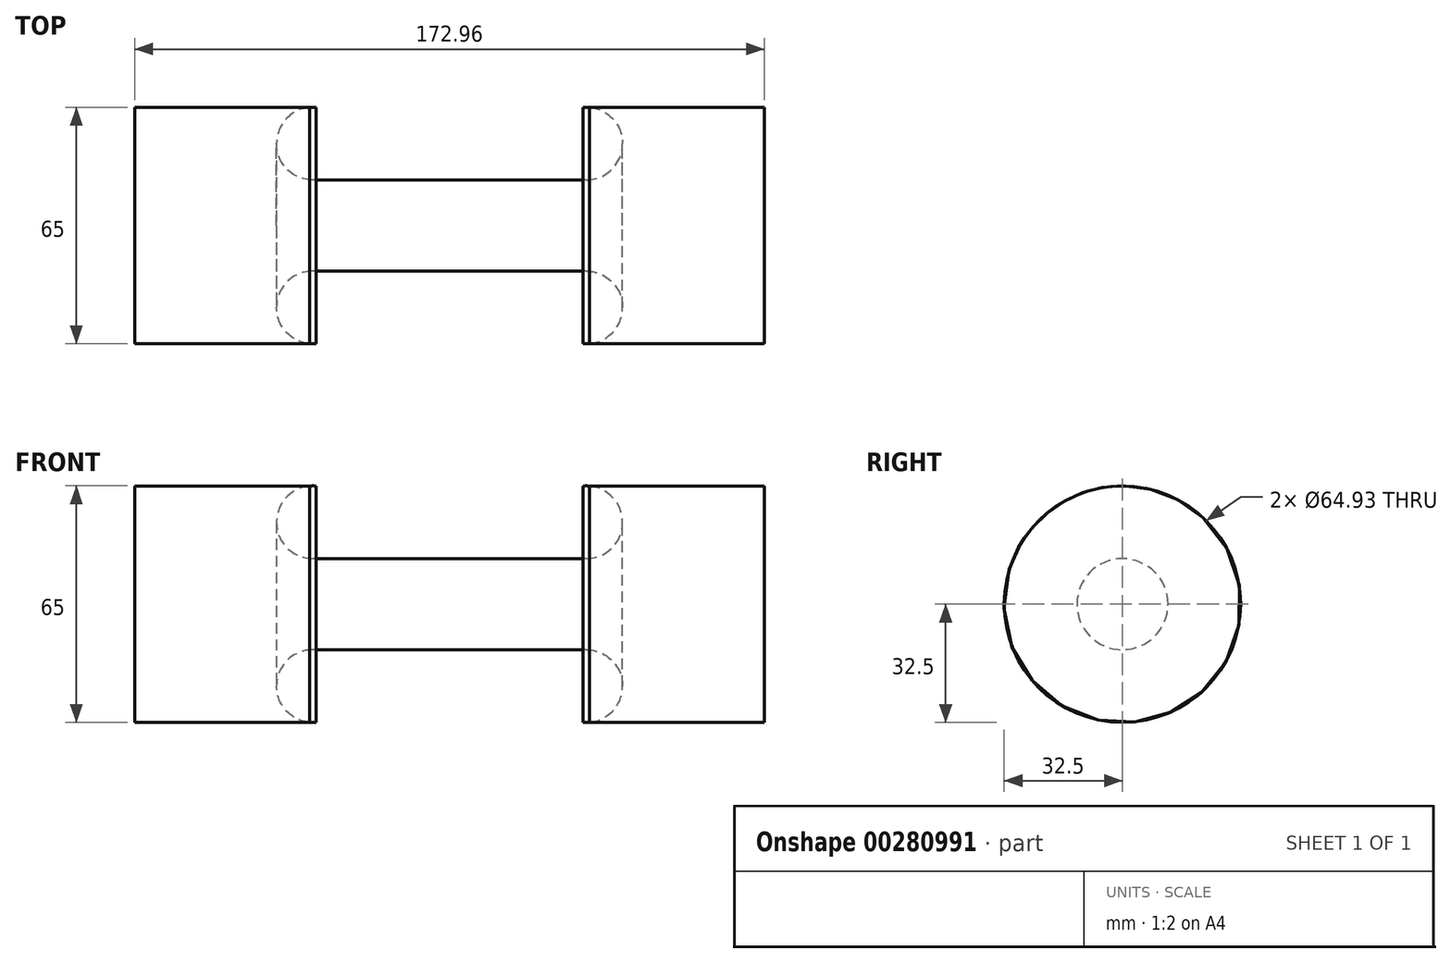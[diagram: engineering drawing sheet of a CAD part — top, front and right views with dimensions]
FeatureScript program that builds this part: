
annotation { "Feature Type Name" : "Feature", "Feature Type Description" : "" }
export const myFeature = defineFeature(function(context is Context, id is Id, definition is map)
    precondition{}
    {
        {
            var Q0;
            Q0=qCreatedBy(makeId("Front.planeOp"),FACE);
            var sketch = newSketch(context, id + "F0", { "sketchPlane" : qUnion([Q0])});
            skLineSegment(sketch, "E0", {"start": v(0, 12.5) * mm, "end": v(37.5, 12.5) * mm});
            skArc(sketch, "E1", {"start": v(37.5, 12.5) * mm, "mid": v(47.5, 22.93) * mm, "end": v(36.64, 32.46) * mm});
            skLineSegment(sketch, "E2", {"start": v(36.64, 32.46) * mm, "end": v(86.48, 32.46) * mm});
            skLineSegment(sketch, "E3", {"start": v(86.48, 32.46) * mm, "end": v(86.48, 0) * mm});
            skArc(sketch, "E4.MirrorCS", {"start": v(-37.5, 12.5) * mm, "mid": v(-47.5, 22.93) * mm, "end": v(-36.64, 32.46) * mm});
            skLineSegment(sketch, "E5.MirrorCS", {"start": v(0, 12.5) * mm, "end": v(-37.5, 12.5) * mm});
            skLineSegment(sketch, "E6.MirrorCS", {"start": v(-86.48, 32.46) * mm, "end": v(-86.48, 0) * mm});
            skLineSegment(sketch, "E7.MirrorCS", {"start": v(-36.64, 32.46) * mm, "end": v(-86.48, 32.46) * mm});
            skLineSegment(sketch, "E8", {"start": v(-86.48, 0) * mm, "end": v(86.48, 0) * mm});
            skSolve(sketch);
        }
        {
            var Q0;
            Q0 = qSketchRegion(id + "F0", true);
            var Q1;
            Q1=sQuery(id+"F0.wireOp",EDGE,"E8");
            revolve(context, id + "F1", {"entities" : qUnion([Q0]), "axis" : qUnion([Q1]), "revolveType" : RevolveType.FULL});
        }
    });
